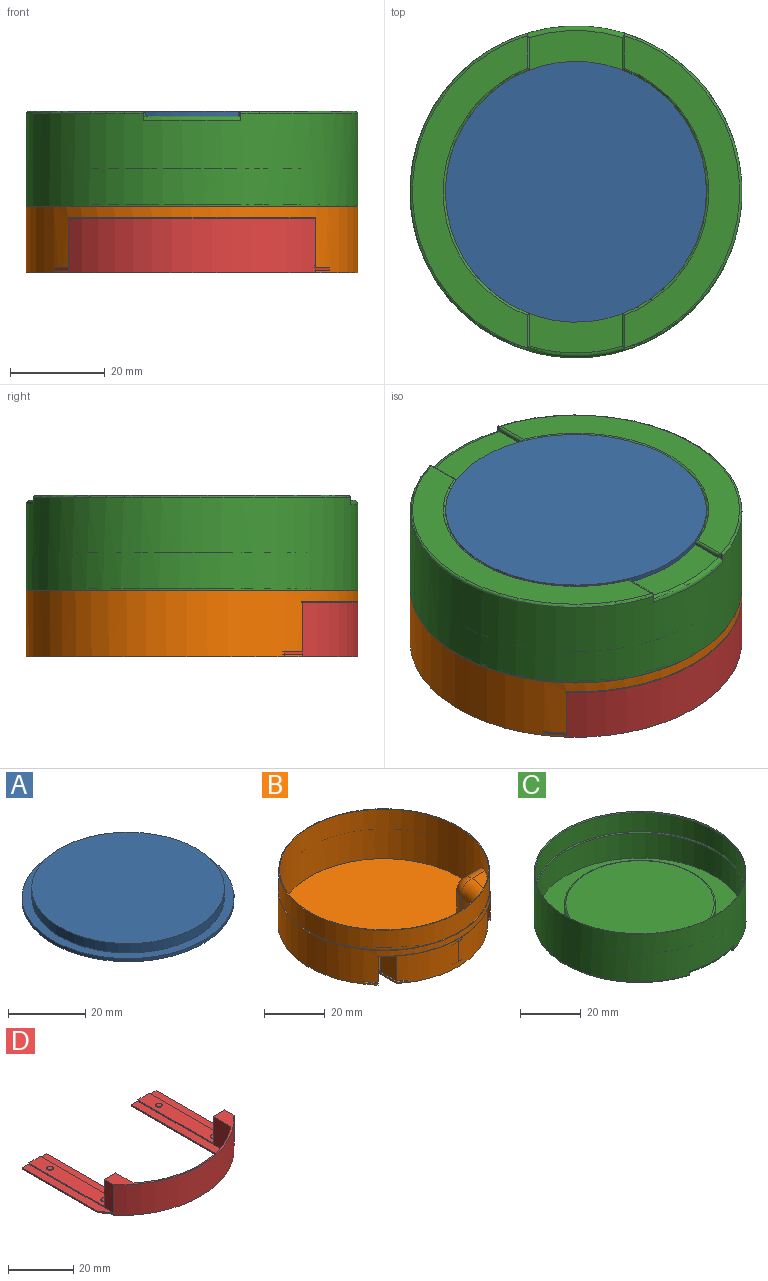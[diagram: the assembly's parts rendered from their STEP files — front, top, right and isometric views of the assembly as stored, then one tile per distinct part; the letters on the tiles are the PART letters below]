
ASSEMBLY  parts=4 mates=3
PART A: 5 faces, bbox 55x55x4 mm
  f0: cylinder r=25mm len=50mm, axis (0,0,-1), area 471.2mm2, adj f1,f3
  f1: plane 50x50mm, normal (0,0,1), area 1963.5mm2, adj f0
  f2: cylinder r=27.5mm len=55mm, axis (0,0,-1), area 172.8mm2, adj f3,f4
  f3: plane 55x55mm, normal (0,0,1), area 412.3mm2, adj f0,f2
  f4: plane 55x55mm, normal (0,0,-1), area 2375.8mm2, adj f2
PART B: 61 faces, bbox 70.1x76.7x22.1 mm
  f0: plane 36.54x3mm, normal (0,0,-1), area 109.6mm2, adj f4,f12,f18,f53
  f1: plane 5.84x3mm, normal (0,0,-1), area 14.3mm2, adj f5,f10,f41,f52
  f2: plane 36.54x3mm, normal (0,0,-1), area 104.4mm2, adj f8,f11,f23,f31,f55
  f3: plane 70x69.54mm, normal (0,0,-1), area 3432mm2, adj f8,f9,f13,f18,f20,f22,f23,f24
  f4: plane 42.47x0.5mm, normal (1,0,0), area 21.2mm2, adj f0,f18,f28,f29,f41,f54
  f5: plane 42.47x0.5mm, normal (-1,0,0), area 21.2mm2, adj f1,f23,f32,f33,f41,f54
  f6: plane 32.63x5mm, normal (0,0,-1), area 160mm2, adj f10,f11,f23,f38,f58
  f7: cylinder r=34.5mm len=69mm, axis (0,0,1), area 3330.3mm2, adj f14,f15,f34,f35,f36,f37,f45,f47
  f8: cylinder r=35mm len=70mm, axis (0,0,-1), area 2382.4mm2, adj f2,f3,f9,f11,f13,f17,f19,f25
  f9: cylinder r=35mm len=3.87mm, axis (0,0,-1), area 2.4mm2, adj f3,f8,f22,f30
  f10: plane 40.27x10.5mm, normal (-1,0,0), area 96.5mm2, adj f1,f6,f23,f32,f38,f39,f41,f52
  f11: plane 36.71x10.78mm, normal (1,0,0), area 58.3mm2, adj f2,f6,f8,f23,f38,f39,f55,f60
  f12: plane 40.27x10.5mm, normal (1,0,0), area 96.5mm2, adj f0,f18,f21,f29,f39,f40,f41,f52
  f13: plane 36.63x0.5mm, normal (-1,0,0), area 18.3mm2, adj f3,f8,f18,f26
  f14: plane 69.5x69.5mm, normal (0,0,1), area 54.4mm2, adj f7,f16
  f15: plane 69x69mm, normal (0,0,1), area 3377.2mm2, adj f7,f34,f35,f42,f43,f44,f49
  f16: cylinder r=34.75mm len=69.5mm, axis (0,0,1), area 1746.7mm2, adj f14,f17
  f17: plane 70x70mm, normal (0,0,1), area 54.8mm2, adj f8,f16
  f18: plane 11x1.5mm, normal (0,-1,0), area 10.5mm2, adj f0,f3,f4,f12,f13,f19,f20,f21
  f19: plane 36.71x10.78mm, normal (-1,0,0), area 58.3mm2, adj f8,f18,f21,f25,f39,f40,f60
  f20: plane 40.27x0.5mm, normal (1,0,0), area 20.1mm2, adj f3,f18,f28,f41
  f21: plane 32.63x5mm, normal (0,0,-1), area 160mm2, adj f12,f18,f19,f40,f56
  f22: plane 36.63x0.5mm, normal (1,0,0), area 18.3mm2, adj f3,f9,f23,f30
  f23: plane 11x1.5mm, normal (0,-1,0), area 10.5mm2, adj f2,f3,f5,f6,f10,f11,f22,f24
  f24: plane 40.27x0.5mm, normal (-1,0,0), area 20.1mm2, adj f3,f23,f33,f41
  f25: plane 36.63x3mm, normal (0,0,-1), area 104.4mm2, adj f8,f18,f19,f27
  f26: plane 36.63x3mm, normal (0,0,1), area 104.4mm2, adj f8,f13,f18,f27
  f27: plane 32.76x0.5mm, normal (-1,0,0), area 16.4mm2, adj f8,f18,f25,f26
  f28: plane 42.47x3mm, normal (0,0,1), area 124.2mm2, adj f4,f18,f20,f41
  f29: plane 5.84x3mm, normal (0,0,-1), area 14.3mm2, adj f4,f12,f41,f52
  f30: plane 36.63x3mm, normal (0,0,1), area 104.4mm2, adj f9,f22,f23,f31
  f31: plane 32.76x0.5mm, normal (1,0,0), area 16.4mm2, adj f2,f8,f23,f30
  f32: plane 36.54x3mm, normal (0,0,-1), area 109.6mm2, adj f5,f10,f23,f53
  f33: plane 42.47x3mm, normal (0,0,1), area 124.2mm2, adj f5,f23,f24,f41
  f34: plane 8.5x7.92mm, normal (0,1,0), area 67.3mm2, adj f7,f15,f48,f49
  f35: plane 8.37x7.92mm, normal (0,1,0), area 66.3mm2, adj f7,f15,f44,f45
  f36: plane 10.92x9.79mm, normal (0,0,1), area 36mm2, adj f7,f48,f51
  f37: plane 10.75x9.56mm, normal (0,0,1), area 34.6mm2, adj f7,f45,f47
  f38: plane 10x5mm, normal (0,-1,0), area 50mm2, adj f6,f10,f11,f39
  f39: plane 52.18x15.47mm, normal (0,0,-1), area 78.3mm2, adj f10,f11,f12,f19,f38,f40,f41,f60
  f40: plane 10x5mm, normal (0,-1,0), area 50mm2, adj f12,f19,f21,f39
  f41: cylinder r=33.15mm len=42.18mm, axis (0,0,-1), area 522mm2, adj f1,f3,f4,f5,f10,f12,f20,f24
  f42: cylinder r=19.63mm len=18.8mm, axis (0,0,1), area 224.6mm2, adj f15,f43,f49,f51
  f43: cylinder r=19.63mm len=18.93mm, axis (0,0,1), area 225.6mm2, adj f15,f42,f44,f47
  f44: cylinder r=5.08mm len=7.92mm, axis (0,0,1), area 59.7mm2, adj f15,f35,f43,f46
  f45: cylinder r=5.08mm len=8.37mm, axis (1,0,0), area 60.5mm2, adj f7,f35,f37,f46
  f46: sphere r=5.08mm, area 38.3mm2, adj f44,f45,f47
  f47: torus R=24.71mm, axis (0,0,1), area 159mm2, adj f7,f37,f43,f46
  f48: cylinder r=5.08mm len=8.5mm, axis (1,0,0), area 61.5mm2, adj f7,f34,f36,f50
  f49: cylinder r=5.08mm len=7.92mm, axis (0,0,1), area 59.7mm2, adj f15,f34,f42,f50
  f50: sphere r=5.08mm, area 38.3mm2, adj f48,f49,f51
  f51: torus R=24.71mm, axis (0,0,1), area 160mm2, adj f7,f36,f42,f50
  f52: plane 42.18x0.45mm, normal (0,1,0), area 19mm2, adj f1,f10,f12,f29,f53,f54
  f53: plane 42.18x0.45mm, normal (0,-0.98,-0.19), area 19.3mm2, adj f0,f10,f12,f32,f52,f54
  f54: plane 36.18x0.09mm, normal (0,0,1), area 3.2mm2, adj f4,f5,f52,f53
  f55: plane 0.45x0.09mm, normal (0,-0.98,-0.19), area 0mm2, adj f2,f8,f11
  f56: cylinder r=1mm len=2mm, axis (0,0,-1), area 0.6mm2, adj f21,f57
  f57: plane 2x2mm, normal (0,0,-1), area 3.1mm2, adj f56
  f58: cylinder r=1mm len=2mm, axis (0,0,-1), area 1.3mm2, adj f6,f59
  f59: plane 2x2mm, normal (0,0,-1), area 3.1mm2, adj f58
  f60: torus R=34.8mm, axis (0,0,-1), area 18.5mm2, adj f8,f11,f19,f39
PART C: 41 faces, bbox 76.3x76.3x20.1 mm
  f0: torus R=34.5mm, axis (0,0,1), area 69.5mm2, adj f6,f12,f31,f33,f37
  f1: torus R=34.5mm, axis (0,0,1), area 69.6mm2, adj f6,f9,f13,f32,f34
  f2: plane 6.36x0.5mm, normal (1,0,0), area 3.2mm2, adj f4,f22,f23,f37
  f3: plane 6.37x0.5mm, normal (-1,0,0), area 3.2mm2, adj f5,f22,f24,f38
  f4: cylinder r=0.5mm len=7.23mm, axis (0,1,0), area 5.3mm2, adj f2,f12,f28,f37
  f5: cylinder r=0.5mm len=7.23mm, axis (0,-1,0), area 5.3mm2, adj f3,f13,f29,f38
  f6: cylinder r=35mm len=70mm, axis (0,0,-1), area 4225.8mm2, adj f0,f1,f20,f31,f32,f33,f34,f39
  f7: plane 6.37x0.5mm, normal (1,0,0), area 3.2mm2, adj f10,f22,f23,f35
  f8: plane 6.44x0.5mm, normal (-1,0,0), area 3.2mm2, adj f11,f22,f24,f36
  f9: cylinder r=34.5mm len=0.11mm, axis (0,0,-1), area 0mm2, adj f1,f11,f32
  f10: cylinder r=0.5mm len=7.23mm, axis (0,1,0), area 5.3mm2, adj f7,f12,f28,f35
  f11: cylinder r=0.5mm len=7.26mm, axis (0,-1,0), area 5.3mm2, adj f8,f9,f13,f29,f32,f36
  f12: plane 65.86x24.21mm, normal (0,0,-1), area 501.8mm2, adj f0,f4,f10,f28,f37
  f13: plane 65.86x24.21mm, normal (0,0,-1), area 501.8mm2, adj f1,f5,f11,f29
  f14: cylinder r=34.75mm len=69.5mm, axis (0,0,1), area 1652.2mm2, adj f20,f21
  f15: plane 69x69mm, normal (0,0,1), area 1775.8mm2, adj f16,f17
  f16: cylinder r=34.5mm len=69mm, axis (0,0,1), area 2182.2mm2, adj f15,f21
  f17: cylinder r=25mm len=50mm, axis (0,0,-1), area 863.9mm2, adj f15,f19
  f18: plane 49x49mm, normal (0,0,1), area 1885.7mm2, adj f19
  f19: torus R=24.5mm, axis (0,0,1), area 122.5mm2, adj f17,f18
  f20: torus R=35.25mm, axis (0,0,1), area 114.6mm2, adj f6,f14
  f21: torus R=35mm, axis (0,0,1), area 113.8mm2, adj f14,f16
  f22: plane 68x55mm, normal (0,0,-1), area 749.3mm2, adj f2,f3,f7,f8,f23,f24,f30,f35
  f23: cylinder r=27.5mm len=51.4mm, axis (0,0,-1), area 33.2mm2, adj f2,f7,f22,f28
  f24: cylinder r=27.5mm len=51.4mm, axis (0,0,-1), area 33.2mm2, adj f3,f8,f22,f29
  f25: plane 47x47mm, normal (0,0,-1), area 1734.9mm2, adj f26
  f26: torus R=23.5mm, axis (0,0,-1), area 117.5mm2, adj f25,f27
  f27: cylinder r=24mm len=48mm, axis (0,0,-1), area 452.4mm2, adj f26,f30
  f28: torus R=28mm, axis (0,0,1), area 52.3mm2, adj f4,f10,f12,f23
  f29: torus R=28mm, axis (0,0,1), area 52.3mm2, adj f5,f11,f13,f24
  f30: torus R=24.5mm, axis (0,0,-1), area 119.3mm2, adj f22,f27
  f31: plane 2x0.52mm, normal (1,0,0), area 0.7mm2, adj f0,f6,f35,f40
  f32: plane 2x0.56mm, normal (-1,0,0), area 0.7mm2, adj f1,f6,f9,f11,f36,f40
  f33: plane 2x0.52mm, normal (1,0,0), area 0.7mm2, adj f0,f6,f37,f39
  f34: plane 2x0.52mm, normal (-1,0,0), area 0.7mm2, adj f1,f6,f38,f39
  f35: cylinder r=1mm len=1.13mm, axis (0,0,-1), area 0.9mm2, adj f7,f10,f22,f31,f40
  f36: cylinder r=1mm len=1.11mm, axis (0,0,-1), area 0.7mm2, adj f8,f11,f22,f32,f40
  f37: cylinder r=1mm len=1.14mm, axis (0,0,-1), area 0.9mm2, adj f0,f2,f4,f12,f22,f33,f39
  f38: cylinder r=1mm len=1.13mm, axis (0,0,-1), area 0.9mm2, adj f3,f5,f22,f34,f39
  f39: torus R=34mm, axis (0,0,-1), area 32.6mm2, adj f6,f22,f33,f34,f37,f38
  f40: torus R=34mm, axis (0,0,-1), area 32.4mm2, adj f6,f22,f31,f32,f35,f36
PART D: 46 faces, bbox 58x48.3x11.5 mm
  f0: plane 36.6x10.5mm, normal (1,0,0), area 56.7mm2, adj f2,f9,f12,f19,f25,f30,f33
  f1: plane 40.23x10.8mm, normal (0,0,1), area 217.3mm2, adj f13,f15,f20,f21,f22,f23,f26,f34
  f2: plane 40.23x10.8mm, normal (0,0,1), area 217.5mm2, adj f0,f6,f17,f25,f27,f28,f29,f32
  f3: plane 36.6x2.9mm, normal (0,0,-1), area 100.3mm2, adj f6,f7,f25,f29
  f4: plane 40.23x2.9mm, normal (0,0,-1), area 116.7mm2, adj f10,f20,f22,f23
  f5: plane 36.6x2.9mm, normal (0,0,-1), area 100.1mm2, adj f11,f20,f21,f26
  f6: plane 32.6x0.5mm, normal (1,0,0), area 16.3mm2, adj f2,f3,f25,f29
  f7: plane 36.6x0.5mm, normal (1,0,0), area 18.3mm2, adj f3,f12,f18,f25
  f8: plane 40.23x0.5mm, normal (-1,0,0), area 20.1mm2, adj f16,f18,f24,f25
  f9: plane 10.05x5mm, normal (0,1,0), area 50.3mm2, adj f0,f17,f19,f30
  f10: plane 40.23x0.5mm, normal (1,0,0), area 20.1mm2, adj f4,f16,f18,f20
  f11: plane 36.6x0.5mm, normal (-1,0,0), area 18.3mm2, adj f5,f12,f18,f20
  f12: cylinder r=35mm len=52.18mm, axis (0,0,1), area 677.2mm2, adj f0,f7,f11,f13,f18,f19,f26,f29
  f13: plane 36.6x10.5mm, normal (-1,0,0), area 55mm2, adj f1,f12,f14,f19,f20,f31,f34
  f14: plane 10.1x5mm, normal (0,1,0), area 50.5mm2, adj f13,f15,f19,f31
  f15: plane 40.23x10.5mm, normal (1,0,0), area 93.2mm2, adj f1,f14,f16,f19,f20,f31,f34,f35
  f16: cylinder r=33.15mm len=42.18mm, axis (0,0,1), area 525.8mm2, adj f8,f10,f15,f17,f18,f19,f22,f27
  f17: plane 40.23x10.5mm, normal (-1,0,0), area 94.8mm2, adj f2,f9,f16,f19,f25,f30,f32,f33
  f18: plane 52.18x48.27mm, normal (0,0,-1), area 416.1mm2, adj f7,f8,f10,f11,f12,f16,f20,f25
  f19: plane 52.18x15.67mm, normal (0,0,1), area 90.1mm2, adj f0,f9,f12,f13,f14,f15,f16,f17
  f20: plane 10.8x1.4mm, normal (0,1,0), area 9.9mm2, adj f1,f4,f5,f10,f11,f13,f15,f18
  f21: plane 32.46x0.5mm, normal (-1,0,0), area 16.2mm2, adj f1,f5,f20,f26
  f22: plane 2.9x0.5mm, normal (0,-1,0), area 1.4mm2, adj f1,f4,f16,f23
  f23: plane 40.23x0.5mm, normal (1,0,0), area 20.1mm2, adj f1,f4,f20,f22
  f24: plane 40.23x2.9mm, normal (0,0,-1), area 116.7mm2, adj f8,f25,f27,f28
  f25: plane 10.8x1.45mm, normal (0,1,0), area 10.1mm2, adj f0,f2,f3,f6,f7,f8,f17,f18
  f26: plane 4.14x2.9mm, normal (-0.82,-0.57,0), area 2.5mm2, adj f1,f5,f12,f21
  f27: plane 2.9x0.5mm, normal (0,-1,0), area 1.4mm2, adj f2,f16,f24,f28
  f28: plane 40.23x0.5mm, normal (-1,0,0), area 20.1mm2, adj f2,f24,f25,f27
  f29: plane 4x2.9mm, normal (0.81,-0.59,0), area 2.5mm2, adj f2,f3,f6,f12
  f30: plane 32.6x5mm, normal (0,0,1), area 156.7mm2, adj f0,f9,f17,f25,f40,f44
  f31: plane 32.6x5mm, normal (0,0,1), area 156.7mm2, adj f13,f14,f15,f20,f37,f41
  f32: plane 5x0.45mm, normal (0,1,0), area 2.3mm2, adj f2,f12,f17,f33
  f33: plane 5x0.45mm, normal (0,-0.98,-0.19), area 2.3mm2, adj f0,f2,f17,f32
  f34: plane 5x0.45mm, normal (0,-0.98,-0.19), area 2.3mm2, adj f1,f13,f15,f35
  f35: plane 5x0.45mm, normal (0,1,0), area 2.2mm2, adj f1,f12,f15,f34
  f36: plane 1.8x1.8mm, normal (0,0,1), area 2.5mm2, adj f40
  f37: cylinder r=1mm len=2mm, axis (0,0,-1), area 0.3mm2, adj f31,f39
  f38: plane 1.8x1.8mm, normal (0,0,1), area 2.5mm2, adj f39
  f39: torus R=0.9mm, axis (0,0,1), area 1mm2, adj f37,f38
  f40: torus R=0.9mm, axis (0,0,1), area 1mm2, adj f30,f36
  f41: cylinder r=1mm len=2mm, axis (0,0,-1), area 0.3mm2, adj f31,f45
  f42: plane 1.8x1.8mm, normal (0,0,1), area 2.5mm2, adj f45
  f43: plane 1.8x1.8mm, normal (0,0,1), area 2.5mm2, adj f44
  f44: torus R=0.9mm, axis (0,0,1), area 1mm2, adj f30,f43
  f45: torus R=0.9mm, axis (0,0,1), area 1mm2, adj f41,f42
PLACE A rot(axis=(1,0,0),180deg) t=(-66.3,-161.22,-24.18)mm
PLACE B t=(-66.3,-161.22,-58.18)mm
PLACE C rot(axis=(1,0,0),180deg) t=(-66.3,-161.22,-24.18)mm
PLACE D t=(-66.3,-161.19,-58.18)mm
MATE slider C.f0 <-> B.f16  axis (0,0,1) through (-66.3,-161.22,-44.18)mm
MATE slider D.f25 <-> B.f18  axis (0,-1,0) through (-40.21,-147.92,-58.18)mm
MATE slider A.f2 <-> C.f26  axis (0,0,1) through (-66.3,-161.22,-24.18)mm
